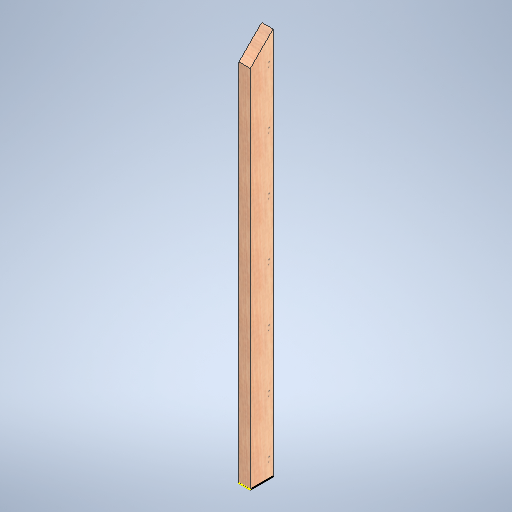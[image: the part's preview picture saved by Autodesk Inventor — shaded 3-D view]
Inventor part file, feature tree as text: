
AUTODESK INVENTOR PART (.ipt)
format: ipt  version: 2025 (Build 290162000, 162)  size: 309,248 bytes
history: native  units: in
note: dims shown in document units (in); Inventor stores cm internally (conversion verified against a paired STEP export)
features: sketch x3, extrude x2
ambient origin geometry x8: Origin, YZ Plane, XZ Plane, XY Plane, X Axis, Y Axis, Z Axis, Center Point
bodies: Solid1 (feature_tree)
feature tree (5):
  extrude  "Extrusion1"  Depth=4.0in
  extrude  "Extrusion2"  TaperAngle=45.0deg  [1 undecoded]
  sketch  "Sketch3"  dims[d5=2.0in d6=0.0in d7=0.5in d8=0.0344in]
  sketch  "Sketch1"  dims[d0=2.0in d1=4.0in]
  sketch  "Sketch2"  dims[d2=68.0in d3=0.0in d4=45.0deg]
note: 1 required parameter value undecoded (feature->parameter linkage not recoverable at this tier; creation-order binding heuristic only, values carry confidence <= 0.55)
